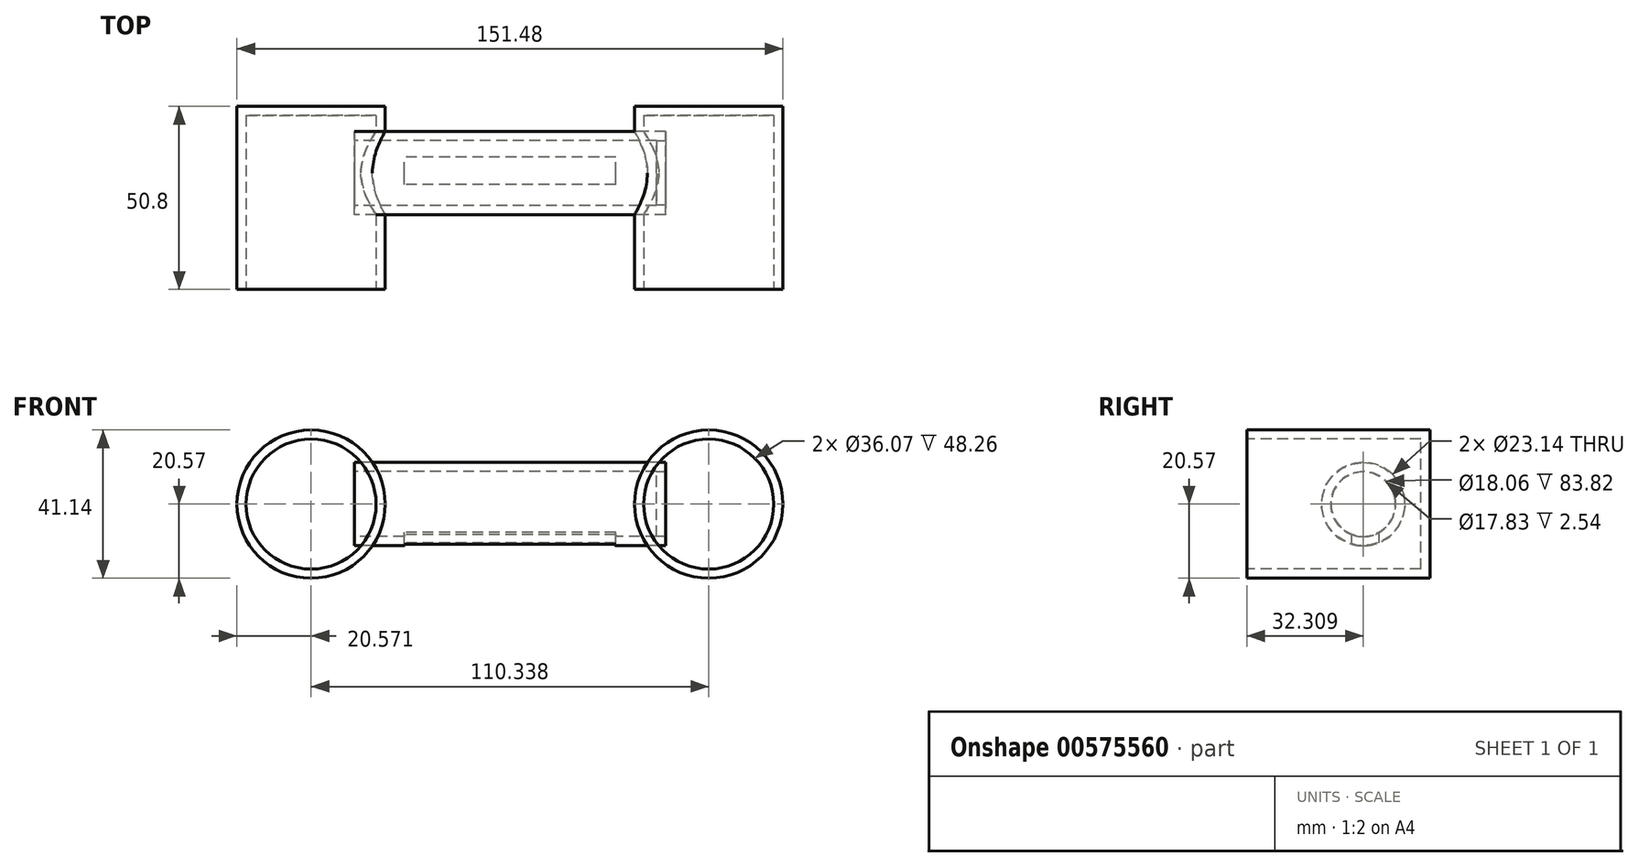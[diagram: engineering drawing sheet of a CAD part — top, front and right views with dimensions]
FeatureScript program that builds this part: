
annotation { "Feature Type Name" : "Feature", "Feature Type Description" : "" }
export const myFeature = defineFeature(function(context is Context, id is Id, definition is map)
    precondition{}
    {
        {
            var Q0;
            Q0=qCreatedBy(makeId("Front.planeOp"),FACE);
            var sketch = newSketch(context, id + "F0", { "sketchPlane" : qUnion([Q0])});
            skCircle(sketch, "E0", {"center": v(-55.17, 0) * mm, "radius": 20.57 * mm});
            skCircle(sketch, "E1.MirrorC", {"center": v(55.17, 0) * mm, "radius": 20.57 * mm});
            skSolve(sketch);
        }
        {
            var Q0;
            Q0 = qSketchRegion(id + "F0", true);
            extrude(context, id + "F1", {"entities" : qUnion([Q0]), "depth" : -50.8 * mm, "offsetDistance" : 25.4 * mm});
        }
        {
            var Q0;
            Q0=makeQuery(id+"F1.opExtrude","CAP_FACE",FACE,{"disambiguationData":[OSD([sQuery(id+"F0.wireOp",EDGE,"E0")])],"isStart":true});
            var Q1;
            Q1=makeQuery(id+"F1.opExtrude","CAP_FACE",FACE,{"disambiguationData":[OSD([sQuery(id+"F0.wireOp",EDGE,"E1.MirrorC")])],"isStart":true});
            shell(context, id + "F2", {"entities" : qUnion([Q0, Q1]), "thickness" : 2.54 * mm});
        }
        {
            var Q0;
            Q0=qCreatedBy(makeId("Right.planeOp"),FACE);
            var sketch = newSketch(context, id + "F3", { "sketchPlane" : qUnion([Q0])});
            skCircle(sketch, "E2", {"center": v(32.3, 0) * mm, "radius": 11.57 * mm});
            skSolve(sketch);
        }
        {
            var Q0;
            Q0=makeQuery(id+"F3.imprint","IMPRINT",FACE,{"disambiguationData":[TD([[makeQuery(id+"F3.imprint","IMPRINT",EDGE,{"derivedFrom":sQuery(id+"F3.wireOp",EDGE,"E2")}),1.0]])]});
            extrude(context, id + "F4", {"entities" : qUnion([Q0]), "operationType" : NewBodyOperationType.REMOVE, "depth" : 50.8 * mm, "offsetDistance" : 25.4 * mm, "hasSecondDirection" : true, "secondDirectionOppositeDirection" : true, "secondDirectionDepth" : 50.8 * mm});
        }
        {
            var Q0;
            Q0=makeQuery(id+"F3.imprint","IMPRINT",FACE,{"disambiguationData":[TD([[makeQuery(id+"F3.imprint","IMPRINT",EDGE,{"derivedFrom":sQuery(id+"F3.wireOp",EDGE,"E2")}),1.0]])]});
            extrude(context, id + "F5", {"entities" : qUnion([Q0]), "depth" : 43.18 * mm, "offsetDistance" : 25.4 * mm, "hasSecondDirection" : true, "secondDirectionOppositeDirection" : true, "secondDirectionDepth" : 43.18 * mm});
        }
        {
            var Q0;
            Q0=makeQuery(id+"F5.opExtrude","CAP_FACE",FACE,{"disambiguationData":[OSD([sQuery(id+"F3.wireOp",EDGE,"E2")])],"isStart":true});
            shell(context, id + "F6", {"entities" : qUnion([Q0]), "thickness" : 2.54 * mm});
        }
        {
            var Q0;
            Q0=sQuery(id+"F3.wireOp",VERTEX,"E2.center");
            var Q1;
            Q1=makeQuery(id+"F5.opExtrude","SWEPT_BODY",BODY,{"disambiguationData":[OSD([sQuery(id+"F3.wireOp",EDGE,"E2")])]});
            hole(context, id + "F7", {"style" : HoleStyle.SIMPLE, "endStyle" : HoleEndStyle.THROUGH, "oppositeDirection" : true, "holeDiameter" : 17.83 * mm, "isTappedThrough" : true, "tappedDepth" : 12.7 * mm, "tapClearance" : 3, "startFromSketch" : true, "locations" : qUnion([Q0]), "scope" : qUnion([Q1])});
        }
        {
            var Q0;
            Q0=qCreatedBy(makeId("Top.planeOp"),FACE);
            var sketch = newSketch(context, id + "F8", { "sketchPlane" : qUnion([Q0])});
            skLineSegment(sketch, "E3.bottom", {"start": v(0, 29.1) * mm, "end": v(-29.36, 29.1) * mm});
            skLineSegment(sketch, "E3.top", {"start": v(0, 36.73) * mm, "end": v(-29.36, 36.73) * mm});
            skLineSegment(sketch, "E3.right", {"start": v(-29.36, 29.1) * mm, "end": v(-29.36, 36.73) * mm});
            skLineSegment(sketch, "E4.MirrorCS", {"start": v(0, 36.73) * mm, "end": v(29.36, 36.73) * mm});
            skLineSegment(sketch, "E5.MirrorCS", {"start": v(0, 29.1) * mm, "end": v(29.36, 29.1) * mm});
            skLineSegment(sketch, "E6.MirrorCS", {"start": v(29.36, 29.1) * mm, "end": v(29.36, 36.73) * mm});
            skPoint(sketch, "E7.MirrorCS.end.orphan", {"position": v(0, 36.73) * mm});
            skPoint(sketch, "E7.MirrorCS.start.orphan", {"position": v(0, 29.1) * mm});
            skSolve(sketch);
        }
        {
            var Q0;
            Q0=makeQuery(id+"F8.imprint","IMPRINT",FACE,{"disambiguationData":[TD([[makeQuery(id+"F8.imprint","IMPRINT",EDGE,{"derivedFrom":sQuery(id+"F8.wireOp",EDGE,"E3.bottom")}),-1.0]])]});
            extrude(context, id + "F9", {"entities" : qUnion([Q0]), "operationType" : NewBodyOperationType.REMOVE, "oppositeDirection" : true, "depth" : 12.7 * mm, "offsetDistance" : 25.4 * mm});
        }
    });
